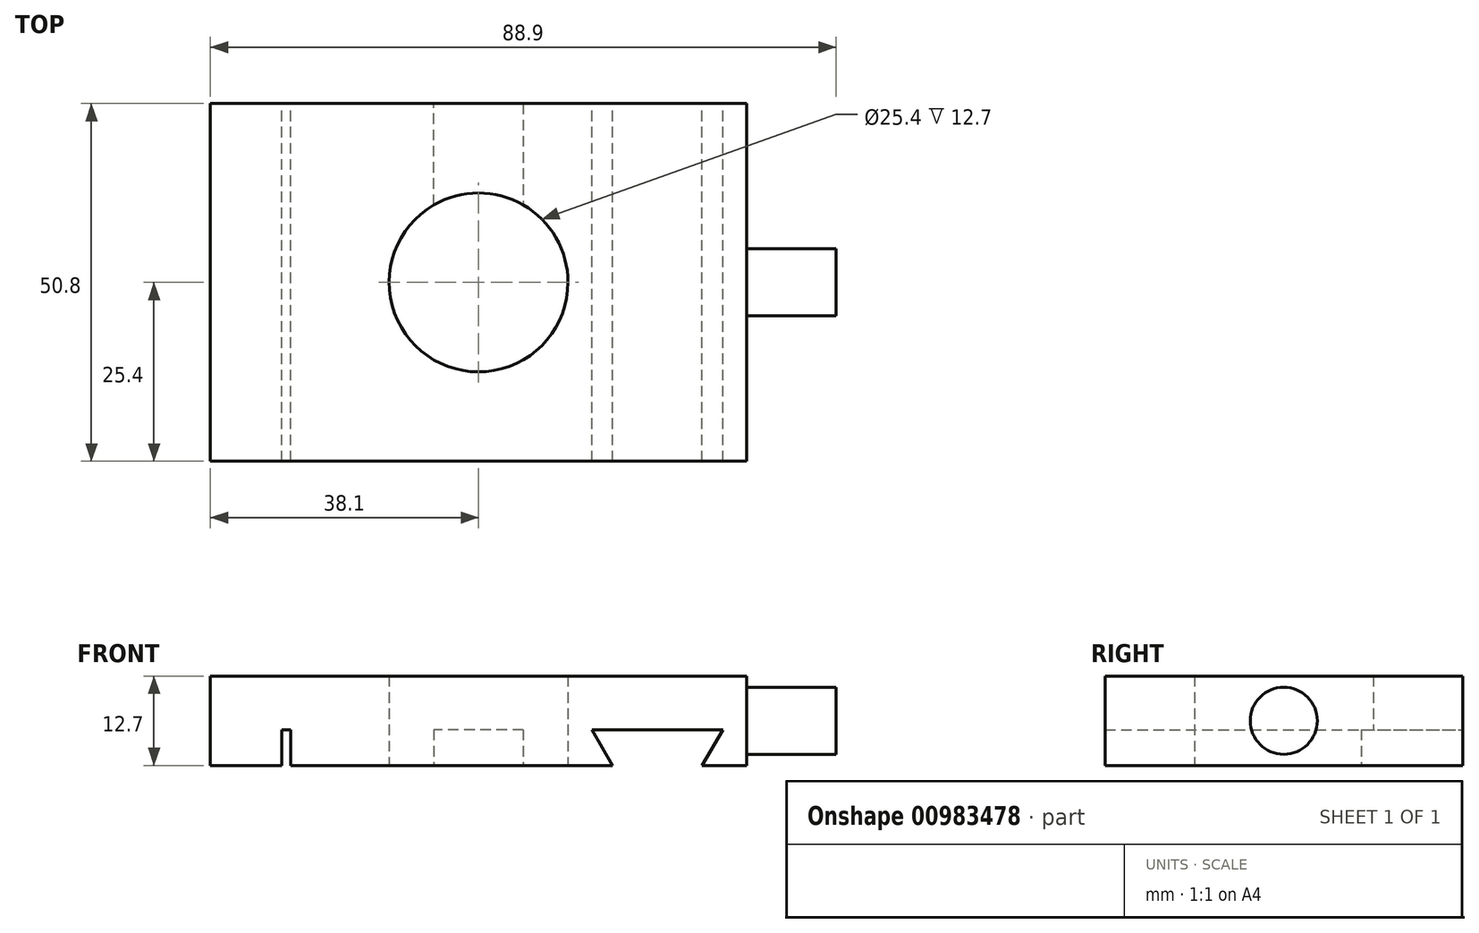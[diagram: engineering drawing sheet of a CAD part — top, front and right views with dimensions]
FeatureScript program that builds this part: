
annotation { "Feature Type Name" : "Feature", "Feature Type Description" : "" }
export const myFeature = defineFeature(function(context is Context, id is Id, definition is map)
    precondition{}
    {
        {
            var Q0;
            Q0=qCreatedBy(makeId("Top.planeOp"),FACE);
            var sketch = newSketch(context, id + "F0", { "sketchPlane" : qUnion([Q0])});
            skLineSegment(sketch, "E0.bottom", {"start": v(38.1, -25.4) * mm, "end": v(-38.1, -25.4) * mm});
            skLineSegment(sketch, "E0.top", {"start": v(38.1, 25.4) * mm, "end": v(-38.1, 25.4) * mm});
            skLineSegment(sketch, "E0.left", {"start": v(38.1, -25.4) * mm, "end": v(38.1, 25.4) * mm});
            skLineSegment(sketch, "E0.right", {"start": v(-38.1, -25.4) * mm, "end": v(-38.1, 25.4) * mm});
            skPoint(sketch, "E0.middle", {"position": v(0, 0) * mm});
            skCircle(sketch, "E1", {"center": v(0, 0) * mm, "radius": 12.7 * mm});
            skSolve(sketch);
        }
        {
            var Q0;
            Q0=makeQuery(id+"F0.imprint","IMPRINT",FACE,{"disambiguationData":[TD([[makeQuery(id+"F0.imprint","IMPRINT",EDGE,{"derivedFrom":sQuery(id+"F0.wireOp",EDGE,"E0.bottom")}),-1.0]])]});
            extrude(context, id + "F1", {"entities" : qUnion([Q0]), "depth" : 12.7 * mm, "offsetDistance" : 25.4 * mm});
        }
        {
            var Q0;
            Q0=makeQuery(id+"F1.opExtrude","CAP_FACE",FACE,{"disambiguationData":[OSD([sQuery(id+"F0.wireOp",EDGE,"E0.bottom"),sQuery(id+"F0.wireOp",EDGE,"E0.top"),sQuery(id+"F0.wireOp",EDGE,"E0.left"),sQuery(id+"F0.wireOp",EDGE,"E0.right"),sQuery(id+"F0.wireOp",EDGE,"E1")])],"isStart":true});
            var sketch = newSketch(context, id + "F2", { "sketchPlane" : qUnion([Q0])});
            skLineSegment(sketch, "E2.bottom", {"start": v(-27.94, 25.4) * mm, "end": v(-26.67, 25.4) * mm});
            skLineSegment(sketch, "E2.top", {"start": v(-27.94, -25.4) * mm, "end": v(-26.67, -25.4) * mm});
            skLineSegment(sketch, "E2.left", {"start": v(-27.94, 25.4) * mm, "end": v(-27.94, -25.4) * mm});
            skLineSegment(sketch, "E2.right", {"start": v(-26.67, 25.4) * mm, "end": v(-26.67, -25.4) * mm});
            skLineSegment(sketch, "E3", {"start": v(-6.35, 25.4) * mm, "end": v(-6.35, -25.4) * mm});
            skLineSegment(sketch, "E4", {"start": v(-6.35, -25.4) * mm, "end": v(6.35, -25.4) * mm});
            skLineSegment(sketch, "E5", {"start": v(6.35, -25.4) * mm, "end": v(6.35, 25.4) * mm});
            skLineSegment(sketch, "E6", {"start": v(6.35, 25.4) * mm, "end": v(-6.35, 25.4) * mm});
            skLineSegment(sketch, "E7", {"start": v(-6.35, 25.4) * mm, "end": v(6.35, 25.4) * mm});
            skPoint(sketch, "E8", {"position": v(0, 0) * mm});
            skLineSegment(sketch, "E9", {"start": v(0, 25.4) * mm, "end": v(0, -25.4) * mm, "construction": true});
            skSolve(sketch);
        }
        {
            var Q0;
            Q0=makeQuery(id+"F2.imprint","IMPRINT",FACE,{"disambiguationData":[TD([[makeQuery(id+"F2.imprint","IMPRINT",EDGE,{"derivedFrom":sQuery(id+"F2.wireOp",EDGE,"E2.bottom")}),1.0]])]});
            var Q1;
            {var subQ0=sQuery(id+"F2.wireOp",EDGE,"E7");Q1=makeQuery(id+"F2.imprint","IMPRINT",FACE,{"disambiguationData":[TD([[makeQuery(id+"F2.imprint","IMPRINT",EDGE,{"derivedFrom":subQ0}),1.0]])]});}
            var Q2;
            {var subQ0=sQuery(id+"F2.wireOp",EDGE,"E4");Q2=makeQuery(id+"F2.imprint","IMPRINT",FACE,{"disambiguationData":[TD([[makeQuery(id+"F2.imprint","IMPRINT",EDGE,{"derivedFrom":subQ0}),-1.0]])]});}
            extrude(context, id + "F3", {"entities" : qUnion([Q0, Q1, Q2]), "operationType" : NewBodyOperationType.REMOVE, "oppositeDirection" : true, "depth" : 5.08 * mm, "offsetDistance" : 25.4 * mm});
        }
        {
            var Q0;
            Q0=makeQuery(id+"F1.opExtrude","SWEPT_FACE",FACE,{"disambiguationData":[OSD([sQuery(id+"F0.wireOp",EDGE,"E0.top")])]});
            var sketch = newSketch(context, id + "F4", { "sketchPlane" : qUnion([Q0])});
            skLineSegment(sketch, "E10", {"start": v(-19.05, 0) * mm, "end": v(-16.12, 5.08) * mm});
            skLineSegment(sketch, "E11", {"start": v(-16.12, 5.08) * mm, "end": v(-34.68, 5.08) * mm});
            skLineSegment(sketch, "E12", {"start": v(-34.68, 5.08) * mm, "end": v(-31.75, 0) * mm});
            skLineSegment(sketch, "E13", {"start": v(-31.75, 0) * mm, "end": v(-19.05, 0) * mm});
            skLineSegment(sketch, "E14", {"start": v(-25.4, 5.08) * mm, "end": v(-25.4, 0) * mm, "construction": true});
            skSolve(sketch);
        }
        {
            var Q0;
            Q0=makeQuery(id+"F4.imprint","IMPRINT",FACE,{"disambiguationData":[TD([[makeQuery(id+"F4.imprint","IMPRINT",EDGE,{"derivedFrom":sQuery(id+"F4.wireOp",EDGE,"E10")}),1.0]])]});
            extrude(context, id + "F5", {"entities" : qUnion([Q0]), "operationType" : NewBodyOperationType.REMOVE, "endBound" : BoundingType.THROUGH_ALL, "oppositeDirection" : true, "depth" : 25.4 * mm, "offsetDistance" : 25.4 * mm});
        }
        {
            var Q0;
            Q0=makeQuery(id+"F1.opExtrude","SWEPT_FACE",FACE,{"disambiguationData":[OSD([sQuery(id+"F0.wireOp",EDGE,"E0.left")])]});
            var sketch = newSketch(context, id + "F6", { "sketchPlane" : qUnion([Q0])});
            skCircle(sketch, "E15", {"center": v(0, 6.35) * mm, "radius": 4.76 * mm});
            skPoint(sketch, "E15.centerSnap0", {"position": v(0, 0) * mm});
            skPoint(sketch, "E15.centerSnap1", {"position": v(25.4, 6.35) * mm});
            skSolve(sketch);
        }
        {
            var Q0;
            Q0=makeQuery(id+"F6.imprint","IMPRINT",FACE,{"disambiguationData":[TD([[makeQuery(id+"F6.imprint","IMPRINT",EDGE,{"derivedFrom":sQuery(id+"F6.wireOp",EDGE,"E15")}),1.0]])]});
            extrude(context, id + "F7", {"entities" : qUnion([Q0]), "operationType" : NewBodyOperationType.ADD, "depth" : 12.7 * mm, "offsetDistance" : 25.4 * mm});
        }
    });
